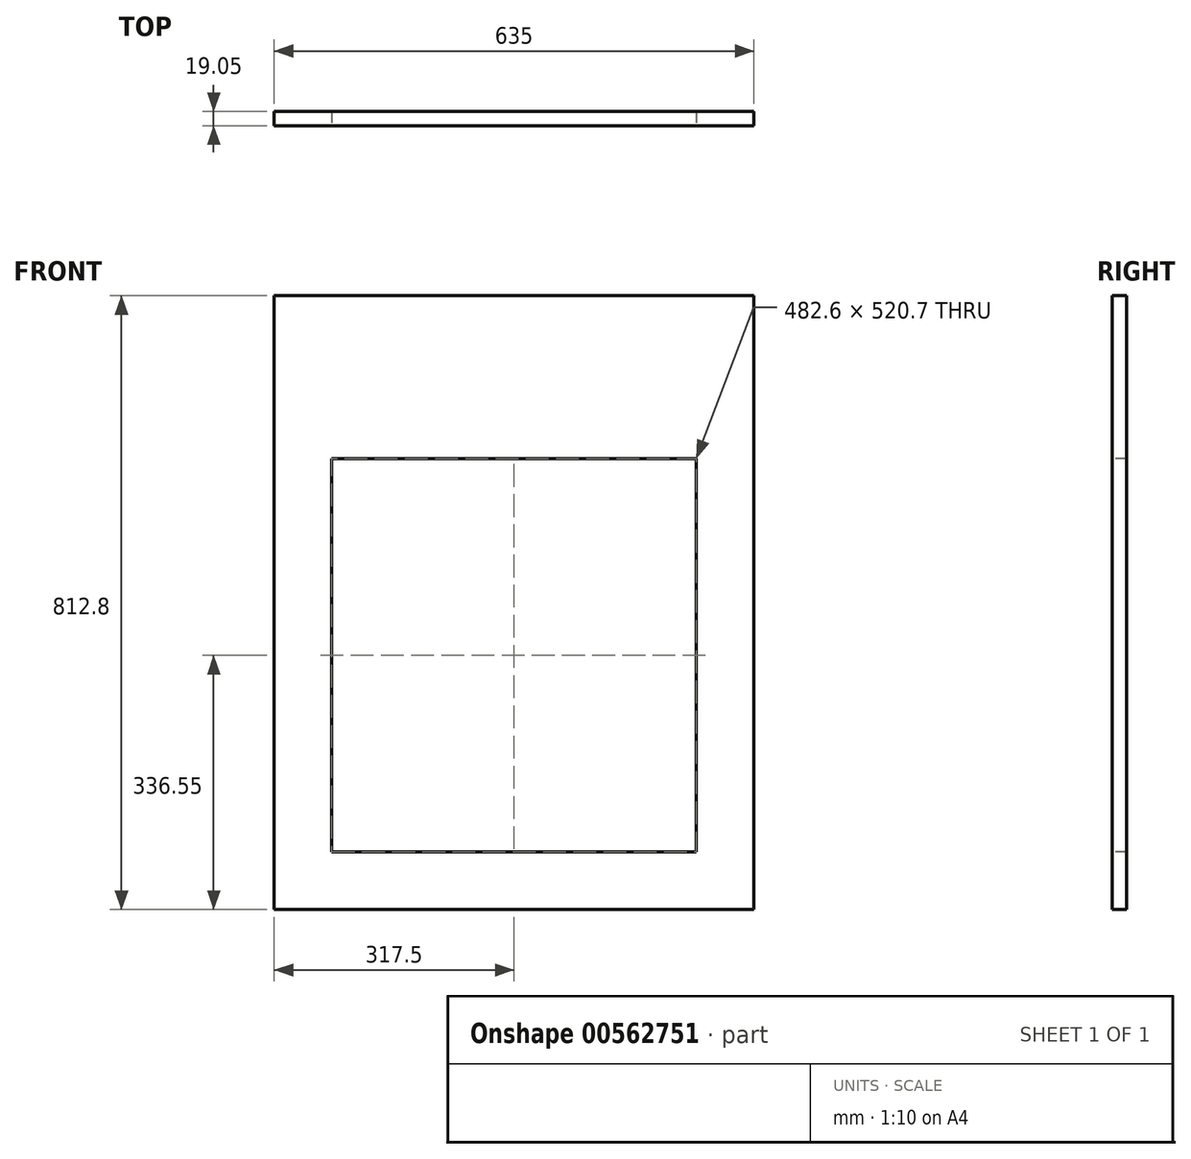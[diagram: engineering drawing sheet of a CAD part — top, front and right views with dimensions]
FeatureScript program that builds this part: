
annotation { "Feature Type Name" : "Feature", "Feature Type Description" : "" }
export const myFeature = defineFeature(function(context is Context, id is Id, definition is map)
    precondition{}
    {
        {
            var Q0;
            Q0=qCreatedBy(makeId("Front.planeOp"),FACE);
            var sketch = newSketch(context, id + "F0", { "sketchPlane" : qUnion([Q0])});
            skLineSegment(sketch, "E0.bottom", {"start": v(317.5, -406.4) * mm, "end": v(-317.5, -406.4) * mm});
            skLineSegment(sketch, "E0.top", {"start": v(317.5, 406.4) * mm, "end": v(-317.5, 406.4) * mm});
            skLineSegment(sketch, "E0.left", {"start": v(317.5, -406.4) * mm, "end": v(317.5, 406.4) * mm});
            skLineSegment(sketch, "E0.right", {"start": v(-317.5, -406.4) * mm, "end": v(-317.5, 406.4) * mm});
            skPoint(sketch, "E0.middle", {"position": v(0, 0) * mm});
            skSolve(sketch);
        }
        {
            var Q0;
            Q0 = qSketchRegion(id + "F0", true);
            extrude(context, id + "F1", {"entities" : qUnion([Q0]), "depth" : 19.05 * mm, "offsetDistance" : 25.4 * mm});
        }
        {
            var Q0;
            Q0=makeQuery(id+"F1.opExtrude","CAP_FACE",FACE,{"disambiguationData":[OSD([sQuery(id+"F0.wireOp",EDGE,"E0.bottom"),sQuery(id+"F0.wireOp",EDGE,"E0.top"),sQuery(id+"F0.wireOp",EDGE,"E0.left"),sQuery(id+"F0.wireOp",EDGE,"E0.right")])],"isStart":false});
            var sketch = newSketch(context, id + "F2", { "sketchPlane" : qUnion([Q0])});
            skLineSegment(sketch, "E1.bottom", {"start": v(-241.3, 190.5) * mm, "end": v(241.3, 190.5) * mm});
            skLineSegment(sketch, "E1.top", {"start": v(-241.3, -330.2) * mm, "end": v(241.3, -330.2) * mm});
            skLineSegment(sketch, "E1.left", {"start": v(-241.3, 190.5) * mm, "end": v(-241.3, -330.2) * mm});
            skLineSegment(sketch, "E1.right", {"start": v(241.3, 190.5) * mm, "end": v(241.3, -330.2) * mm});
            skSolve(sketch);
        }
        {
            var Q0;
            Q0=makeQuery(id+"F2.imprint","IMPRINT",FACE,{"disambiguationData":[TD([[makeQuery(id+"F2.imprint","IMPRINT",EDGE,{"derivedFrom":sQuery(id+"F2.wireOp",EDGE,"E1.bottom")}),-1.0]])]});
            extrude(context, id + "F3", {"entities" : qUnion([Q0]), "operationType" : NewBodyOperationType.REMOVE, "endBound" : BoundingType.THROUGH_ALL, "oppositeDirection" : true, "depth" : 25.4 * mm, "offsetDistance" : 25.4 * mm});
        }
    });
